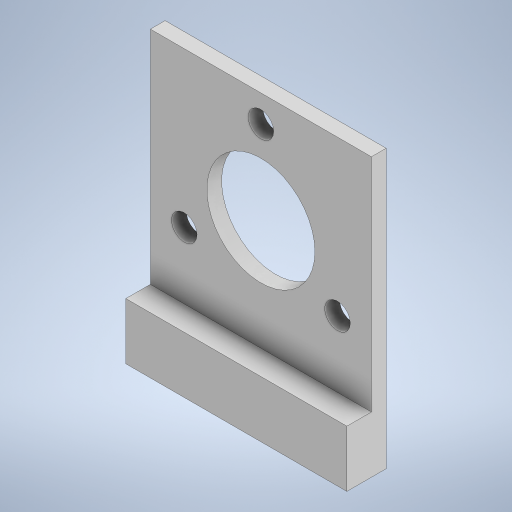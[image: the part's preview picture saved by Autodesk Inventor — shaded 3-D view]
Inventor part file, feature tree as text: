
AUTODESK INVENTOR PART (.ipt)
format: ipt  version: 2024 (Build 280153000, 153)  size: 260,096 bytes
history: native  units: in
note: dims shown in document units (in); Inventor stores cm internally (conversion verified against a paired STEP export)
features: extrude x2, sketch x2
ambient origin geometry x8: Origin, YZ Plane, XZ Plane, XY Plane, X Axis, Y Axis, Z Axis, Center Point
bodies: Body1 (feature_tree)
feature tree (4):
  extrude  "Extrusion2"  Depth=1.7717in
  extrude  "Extrusion5"  Depth=0.6693in
  sketch  "Sketch1"  dims[d0=1.7717in d1=1.7717in]
  sketch  "Sketch12"  dims[d2=0.8661in d3=0.6693in d4=0.6142in d5=120.0deg d6=0.6142in d7=120.0deg d8=0.2047in d9=0.2047in d10=0.2047in d16=0.1181in d17=0.0in d25=1.3386in d26=0.315in d27=0.0in d11=0.0197in d12=0.0344in d13=0.0197in d14=0.0344in]
